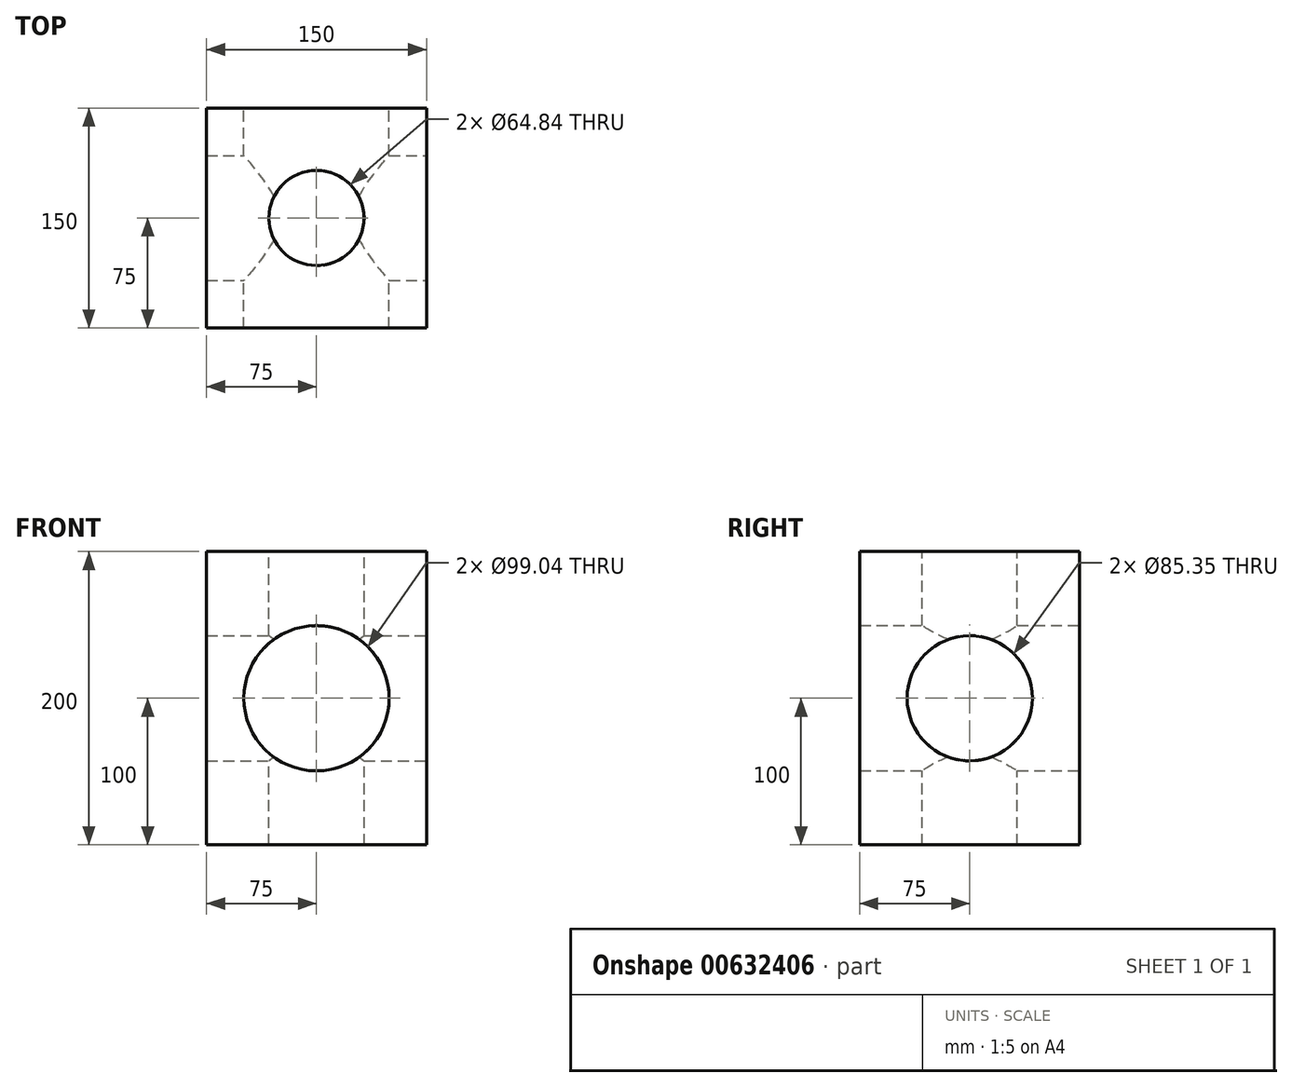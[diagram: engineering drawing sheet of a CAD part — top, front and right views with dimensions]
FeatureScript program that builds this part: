
annotation { "Feature Type Name" : "Feature", "Feature Type Description" : "" }
export const myFeature = defineFeature(function(context is Context, id is Id, definition is map)
    precondition{}
    {
        {
            var Q0;
            Q0=qCreatedBy(makeId("Top.planeOp"),FACE);
            var sketch = newSketch(context, id + "F0", { "sketchPlane" : qUnion([Q0])});
            skLineSegment(sketch, "E0.bottom", {"start": v(-75, 75) * mm, "end": v(75, 75) * mm});
            skLineSegment(sketch, "E0.top", {"start": v(-75, -75) * mm, "end": v(75, -75) * mm});
            skLineSegment(sketch, "E0.left", {"start": v(-75, 75) * mm, "end": v(-75, -75) * mm});
            skLineSegment(sketch, "E0.right", {"start": v(75, 75) * mm, "end": v(75, -75) * mm});
            skLineSegment(sketch, "E1", {"start": v(0, 75) * mm, "end": v(0, 0) * mm, "construction": true});
            skLineSegment(sketch, "E2", {"start": v(0, 0) * mm, "end": v(-75, 0) * mm, "construction": true});
            skSolve(sketch);
        }
        {
            var Q0;
            Q0 = qSketchRegion(id + "F0", true);
            extrude(context, id + "F1", {"entities" : qUnion([Q0]), "endBound" : BoundingType.SYMMETRIC, "depth" : 200 * mm, "offsetDistance" : 25 * mm});
        }
        {
            var Q0;
            Q0=qCreatedBy(makeId("Top.planeOp"),FACE);
            var sketch = newSketch(context, id + "F2", { "sketchPlane" : qUnion([Q0])});
            skCircle(sketch, "E3", {"center": v(0, 0) * mm, "radius": 32.42 * mm});
            skSolve(sketch);
        }
        {
            var Q0;
            Q0 = qSketchRegion(id + "F2", true);
            extrude(context, id + "F3", {"entities" : qUnion([Q0]), "operationType" : NewBodyOperationType.REMOVE, "endBound" : BoundingType.SYMMETRIC, "oppositeDirection" : true, "depth" : 500 * mm, "offsetDistance" : 25 * mm});
        }
        {
            var Q0;
            Q0=qCreatedBy(makeId("Right.planeOp"),FACE);
            var sketch = newSketch(context, id + "F4", { "sketchPlane" : qUnion([Q0])});
            skCircle(sketch, "E4", {"center": v(0, 0) * mm, "radius": 42.68 * mm});
            skSolve(sketch);
        }
        {
            var Q0;
            Q0 = qSketchRegion(id + "F4", true);
            extrude(context, id + "F5", {"entities" : qUnion([Q0]), "operationType" : NewBodyOperationType.REMOVE, "endBound" : BoundingType.SYMMETRIC, "oppositeDirection" : true, "depth" : 500 * mm, "offsetDistance" : 25 * mm});
        }
        {
            var Q0;
            Q0=qCreatedBy(makeId("Front.planeOp"),FACE);
            var sketch = newSketch(context, id + "F6", { "sketchPlane" : qUnion([Q0])});
            skCircle(sketch, "E5", {"center": v(0, 0) * mm, "radius": 49.52 * mm});
            skSolve(sketch);
        }
        {
            var Q0;
            Q0 = qSketchRegion(id + "F6", true);
            extrude(context, id + "F7", {"entities" : qUnion([Q0]), "operationType" : NewBodyOperationType.REMOVE, "endBound" : BoundingType.SYMMETRIC, "depth" : 500 * mm, "offsetDistance" : 25 * mm});
        }
    });
